# Revit family: 9f018811-66de-410e-a4b9-28c31693741d
name_source: partatom
category: Plumbing Fixtures
revit_build: Autodesk Revit 2016 (Build: 20161004_0715(x64)
units: mm (PartAtom-declared; Revit-internal decimal feet)

## family parameters
Cut with Voids When Loaded = No
Host = Face
OmniClass Number = 23.45.05.14.14
OmniClass Title = Sinks/Lavatories
Part Type = Normal
Room Calculation Point = No
Round Connector Dimension = Use Diameter
Shared = No

## types (1)
- ET720
    Assembly Code = D2010400
    CW Connection = No
    Connector Description = Sanitary Drain
    Default Elevation = 4' - 0"
    Description = Ligature Resistant Solid Surface Sink
    Finish = Aluminum - BSP - Anodized-White
    HW Connection = No
    Manufacturer = Behavioral Safety Products
    Model = ET720
    Product Documentation Link = http://besafeprod.com
    Product Page URL = http://besafeprod.com
    Type Image = <None>
    URL = http://besafeprod.com
    Vent Connection = No
    Waste Connection = No
    Water Flow = 0 GPM

## geometry (parser evidence)
native form markers: Blend x4, Sweep x4
no freeform markers — native parametric forms only
